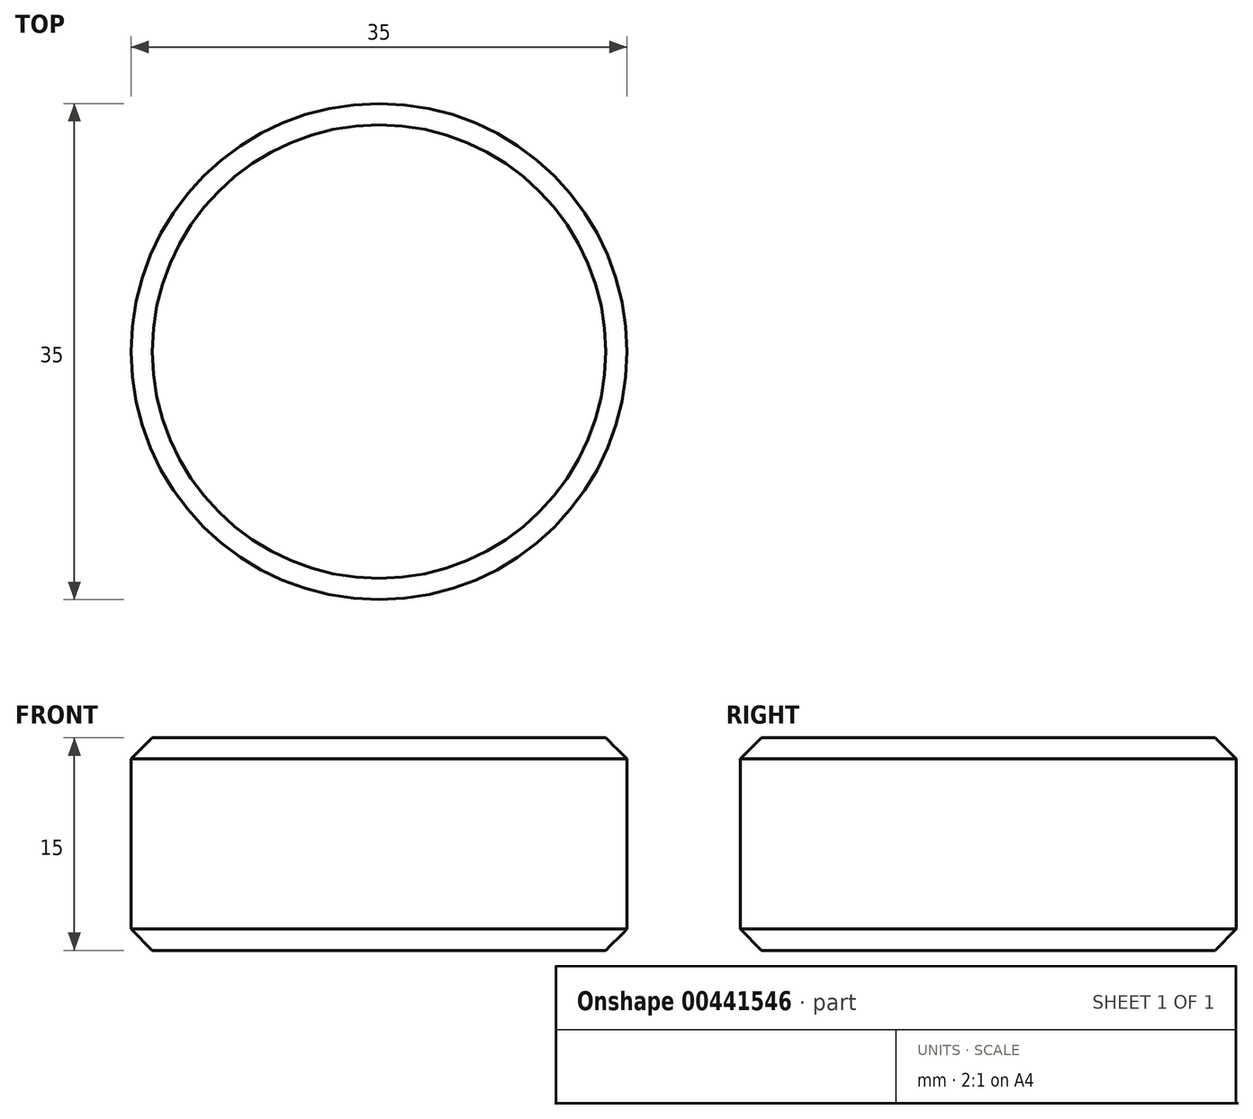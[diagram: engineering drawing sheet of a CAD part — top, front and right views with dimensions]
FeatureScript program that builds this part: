
annotation { "Feature Type Name" : "Feature", "Feature Type Description" : "" }
export const myFeature = defineFeature(function(context is Context, id is Id, definition is map)
    precondition{}
    {
        {
            var Q0;
            Q0=qCreatedBy(makeId("Top.planeOp"),FACE);
            var sketch = newSketch(context, id + "F0", { "sketchPlane" : qUnion([Q0])});
            skCircle(sketch, "E0", {"center": v(-49.02, 3.65) * mm, "radius": 1.5 * mm});
            skCircle(sketch, "E1", {"center": v(0, 0) * mm, "radius": 17.5 * mm});
            skSolve(sketch);
        }
        {
            var Q0;
            Q0=makeQuery(id+"F0.imprint","IMPRINT",FACE,{"disambiguationData":[TD([[makeQuery(id+"F0.imprint","IMPRINT",EDGE,{"derivedFrom":sQuery(id+"F0.wireOp",EDGE,"E0")}),1.0]])]});
            var Q1;
            Q1=makeQuery(id+"F0.imprint","IMPRINT",FACE,{"disambiguationData":[TD([[makeQuery(id+"F0.imprint","IMPRINT",EDGE,{"derivedFrom":sQuery(id+"F0.wireOp",EDGE,"E1")}),1.0]])]});
            extrude(context, id + "F1", {"entities" : qUnion([Q0, Q1]), "depth" : 15 * mm});
        }
        {
            var Q0;
            Q0=makeQuery(id+"F1.opExtrude","CAP_EDGE",EDGE,{"disambiguationData":[OSD([sQuery(id+"F0.wireOp",EDGE,"E0")])],"isStart":false});
            var Q1;
            Q1=makeQuery(id+"F1.opExtrude","CAP_EDGE",EDGE,{"disambiguationData":[OSD([sQuery(id+"F0.wireOp",EDGE,"E1")])],"isStart":false});
            var Q2;
            Q2=makeQuery(id+"F1.opExtrude","SWEPT_FACE",FACE,{"disambiguationData":[OSD([sQuery(id+"F0.wireOp",EDGE,"E1")])]});
            chamfer(context, id + "F2", {"entities" : qUnion([Q0, Q1, Q2]), "width" : 1.5 * mm, "tangentPropagation" : true});
        }
        {
            var Q0;
            Q0=makeQuery(id+"F1.opExtrude","SWEPT_BODY",BODY,{"disambiguationData":[OSD([sQuery(id+"F0.wireOp",EDGE,"E0")])]});
            deleteBodies(context, id + "F3", {"entities" : qUnion([Q0])});
        }
    });
